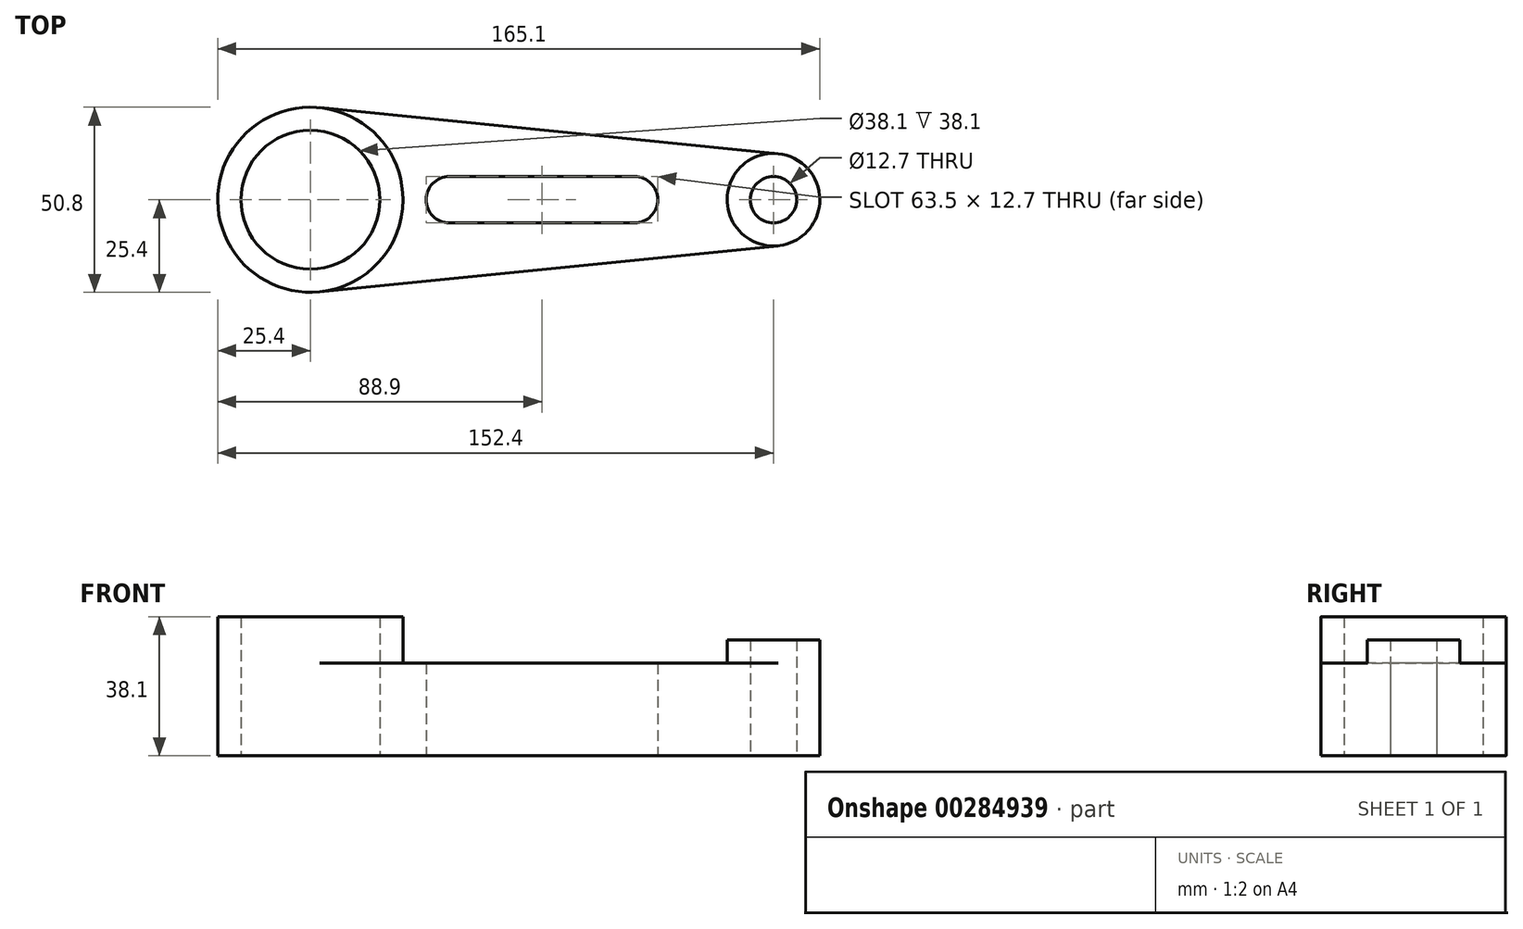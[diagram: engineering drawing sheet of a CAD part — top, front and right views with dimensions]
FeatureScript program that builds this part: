
annotation { "Feature Type Name" : "Feature", "Feature Type Description" : "" }
export const myFeature = defineFeature(function(context is Context, id is Id, definition is map)
    precondition{}
    {
        {
            var Q0;
            Q0=qCreatedBy(makeId("Top.planeOp"),FACE);
            var sketch = newSketch(context, id + "F0", { "sketchPlane" : qUnion([Q0])});
            skArc(sketch, "E0", {"start": v(0, 6.35) * mm, "mid": v(-6.35, 0) * mm, "end": v(0, -6.35) * mm});
            skLineSegment(sketch, "E1.bottom", {"start": v(0, 6.35) * mm, "end": v(50.8, 6.35) * mm});
            skLineSegment(sketch, "E1.top", {"start": v(0, -6.35) * mm, "end": v(50.8, -6.35) * mm});
            skArc(sketch, "E2", {"start": v(50.8, -6.35) * mm, "mid": v(57.15, 0) * mm, "end": v(50.8, 6.35) * mm});
            skPoint(sketch, "E3.endSnap0", {"position": v(-6.35, 0) * mm});
            skCircle(sketch, "E4", {"center": v(-38.1, 0) * mm, "radius": 19.05 * mm});
            skCircle(sketch, "E5", {"center": v(88.9, 0) * mm, "radius": 6.35 * mm});
            skCircle(sketch, "E6", {"center": v(88.9, 0) * mm, "radius": 12.7 * mm});
            skCircle(sketch, "E7", {"center": v(-38.1, 0) * mm, "radius": 25.4 * mm});
            skLineSegment(sketch, "E8", {"start": v(-35.56, 25.27) * mm, "end": v(90.17, 12.64) * mm});
            skLineSegment(sketch, "E9", {"start": v(-35.56, -25.27) * mm, "end": v(90.17, -12.64) * mm});
            skSolve(sketch);
        }
        {
            var Q0;
            Q0=makeQuery(id+"F0.imprint","IMPRINT",FACE,{"disambiguationData":[TD([[makeQuery(id+"F0.imprint","IMPRINT",EDGE,{"derivedFrom":sQuery(id+"F0.wireOp",EDGE,"E0")}),-1.0]])]});
            extrude(context, id + "F1", {"entities" : qUnion([Q0]), "depth" : 25.4 * mm});
        }
        {
            var Q0;
            Q0=makeQuery(id+"F0.imprint","IMPRINT",FACE,{"disambiguationData":[TD([[makeQuery(id+"F0.imprint","IMPRINT",EDGE,{"derivedFrom":sQuery(id+"F0.wireOp",EDGE,"E4")}),-1.0]])]});
            extrude(context, id + "F2", {"entities" : qUnion([Q0]), "operationType" : NewBodyOperationType.ADD, "depth" : 38.1 * mm});
        }
        {
            var Q0;
            Q0=makeQuery(id+"F0.imprint","IMPRINT",FACE,{"disambiguationData":[TD([[makeQuery(id+"F0.imprint","IMPRINT",EDGE,{"derivedFrom":sQuery(id+"F0.wireOp",EDGE,"E5")}),-1.0]])]});
            extrude(context, id + "F3", {"entities" : qUnion([Q0]), "operationType" : NewBodyOperationType.ADD, "depth" : 31.75 * mm});
        }
    });
